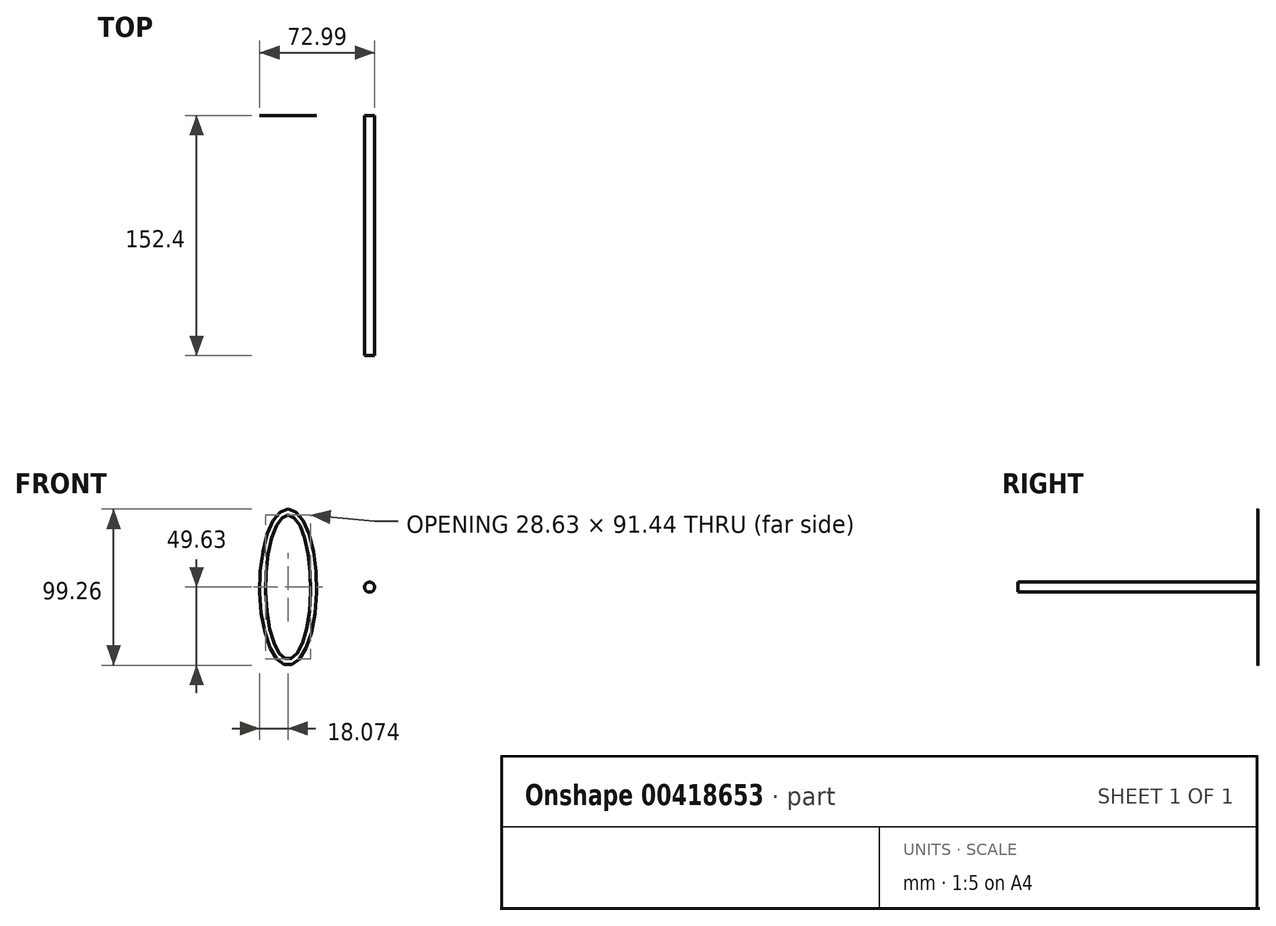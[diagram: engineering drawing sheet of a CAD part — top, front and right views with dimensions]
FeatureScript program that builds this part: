
annotation { "Feature Type Name" : "Feature", "Feature Type Description" : "" }
export const myFeature = defineFeature(function(context is Context, id is Id, definition is map)
    precondition{}
    {
        {
            var Q0;
            Q0=qCreatedBy(makeId("Front.planeOp"),FACE);
            var sketch = newSketch(context, id + "F0", { "sketchPlane" : qUnion([Q0])});
            skCircle(sketch, "E0", {"center": v(0, 0) * mm, "radius": 3.18 * mm});
            skSolve(sketch);
        }
        {
            var Q0;
            Q0 = qSketchRegion(id + "F0", true);
            extrude(context, id + "F1", {"entities" : qUnion([Q0]), "depth" : 152.4 * mm, "offsetDistance" : 25.4 * mm});
        }
        {
            var Q0;
            Q0=qCreatedBy(makeId("Front.planeOp"),FACE);
            var sketch = newSketch(context, id + "F2", { "sketchPlane" : qUnion([Q0])});
            skEllipse(sketch, "E1", {"center": v(-51.74, 0) * mm, "majorRadius": 49.63 * mm, "minorRadius": 18.08 * mm, "majorAxis": v(0, 1)});
            skEllipse(sketch, "E2", {"center": v(-51.74, 0) * mm, "majorRadius": 45.72 * mm, "minorRadius": 14.32 * mm, "majorAxis": v(0, 1)});
            skSolve(sketch);
        }
        {
            var Q0;
            Q0 = qSketchRegion(id + "F2", true);
            extrude(context, id + "F3", {"entities" : qUnion([Q0]), "depth" : 1 / 101.6 * mm});
        }
    });
